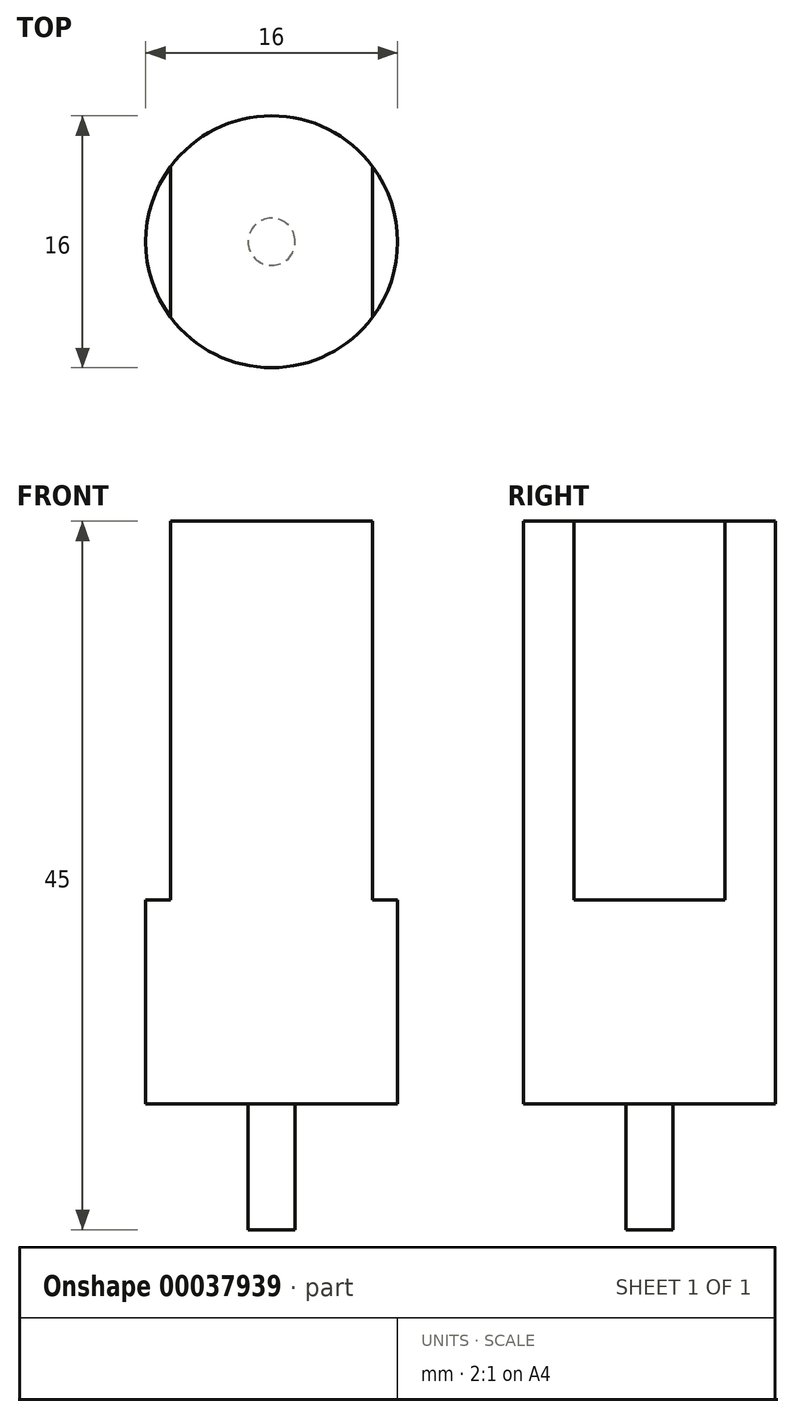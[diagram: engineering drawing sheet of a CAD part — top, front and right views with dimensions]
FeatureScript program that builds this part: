
annotation { "Feature Type Name" : "Feature", "Feature Type Description" : "" }
export const myFeature = defineFeature(function(context is Context, id is Id, definition is map)
    precondition{}
    {
        {
            var Q0;
            Q0=qCreatedBy(makeId("Top.planeOp"),FACE);
            var sketch = newSketch(context, id + "F0", { "sketchPlane" : qUnion([Q0])});
            skCircle(sketch, "E0", {"center": v(0, 0) * mm, "radius": 8 * mm});
            skSolve(sketch);
        }
        {
            var Q0;
            Q0 = qSketchRegion(id + "F0", true);
            extrude(context, id + "F1", {"entities" : qUnion([Q0]), "depth" : 37 * mm});
        }
        {
            var Q0;
            Q0=makeQuery(id+"F1.opExtrude","CAP_FACE",FACE,{"disambiguationData":[OSD([sQuery(id+"F0.wireOp",EDGE,"E0")])],"isStart":true});
            var sketch = newSketch(context, id + "F2", { "sketchPlane" : qUnion([Q0])});
            skCircle(sketch, "E1", {"center": v(0, 0) * mm, "radius": 1.5 * mm});
            skSolve(sketch);
        }
        {
            var Q0;
            Q0 = qSketchRegion(id + "F2", true);
            extrude(context, id + "F3", {"entities" : qUnion([Q0]), "operationType" : NewBodyOperationType.ADD, "depth" : 8 * mm});
        }
        {
            var Q0;
            Q0=makeQuery(id+"F1.opExtrude","CAP_FACE",FACE,{"disambiguationData":[OSD([sQuery(id+"F0.wireOp",EDGE,"E0")])],"isStart":true});
            cPlane(context, id + "F4", {"entities" : qUnion([Q0]), "cplaneType" : CPlaneType.OFFSET, "offset" : 12.95 * mm, "oppositeDirection" : true, "width" : 152.4 * mm, "height" : 152.4 * mm});
        }
        {
            var Q0;
            Q0=makeQuery(id+"F1.opExtrude","CAP_FACE",FACE,{"disambiguationData":[OSD([sQuery(id+"F0.wireOp",EDGE,"E0")])],"isStart":false});
            var sketch = newSketch(context, id + "F5", { "sketchPlane" : qUnion([Q0])});
            skLineSegment(sketch, "E2", {"start": v(-6.41, 4.78) * mm, "end": v(-6.41, -4.78) * mm});
            skLineSegment(sketch, "E3", {"start": v(6.41, 4.78) * mm, "end": v(6.41, -4.78) * mm});
            skArc(sketch, "E4", {"start": v(6.41, -4.78) * mm, "mid": v(8, 0) * mm, "end": v(6.41, 4.78) * mm});
            skArc(sketch, "E5", {"start": v(-6.41, 4.78) * mm, "mid": v(-8, 0) * mm, "end": v(-6.41, -4.78) * mm});
            skLineSegment(sketch, "E6", {"start": v(-6.41, 0) * mm, "end": v(6.41, 0) * mm, "construction": true});
            skSolve(sketch);
        }
        {
            var Q0;
            Q0 = qSketchRegion(id + "F5", true);
            var Q1;
            Q1=qCreatedBy(id+"F4.planeOp",FACE);
            extrude(context, id + "F6", {"entities" : qUnion([Q0]), "operationType" : NewBodyOperationType.REMOVE, "endBound" : BoundingType.UP_TO_SURFACE, "oppositeDirection" : true, "endBoundEntityFace" : qUnion([Q1]), "depth" : 25.4 * mm});
        }
    });
